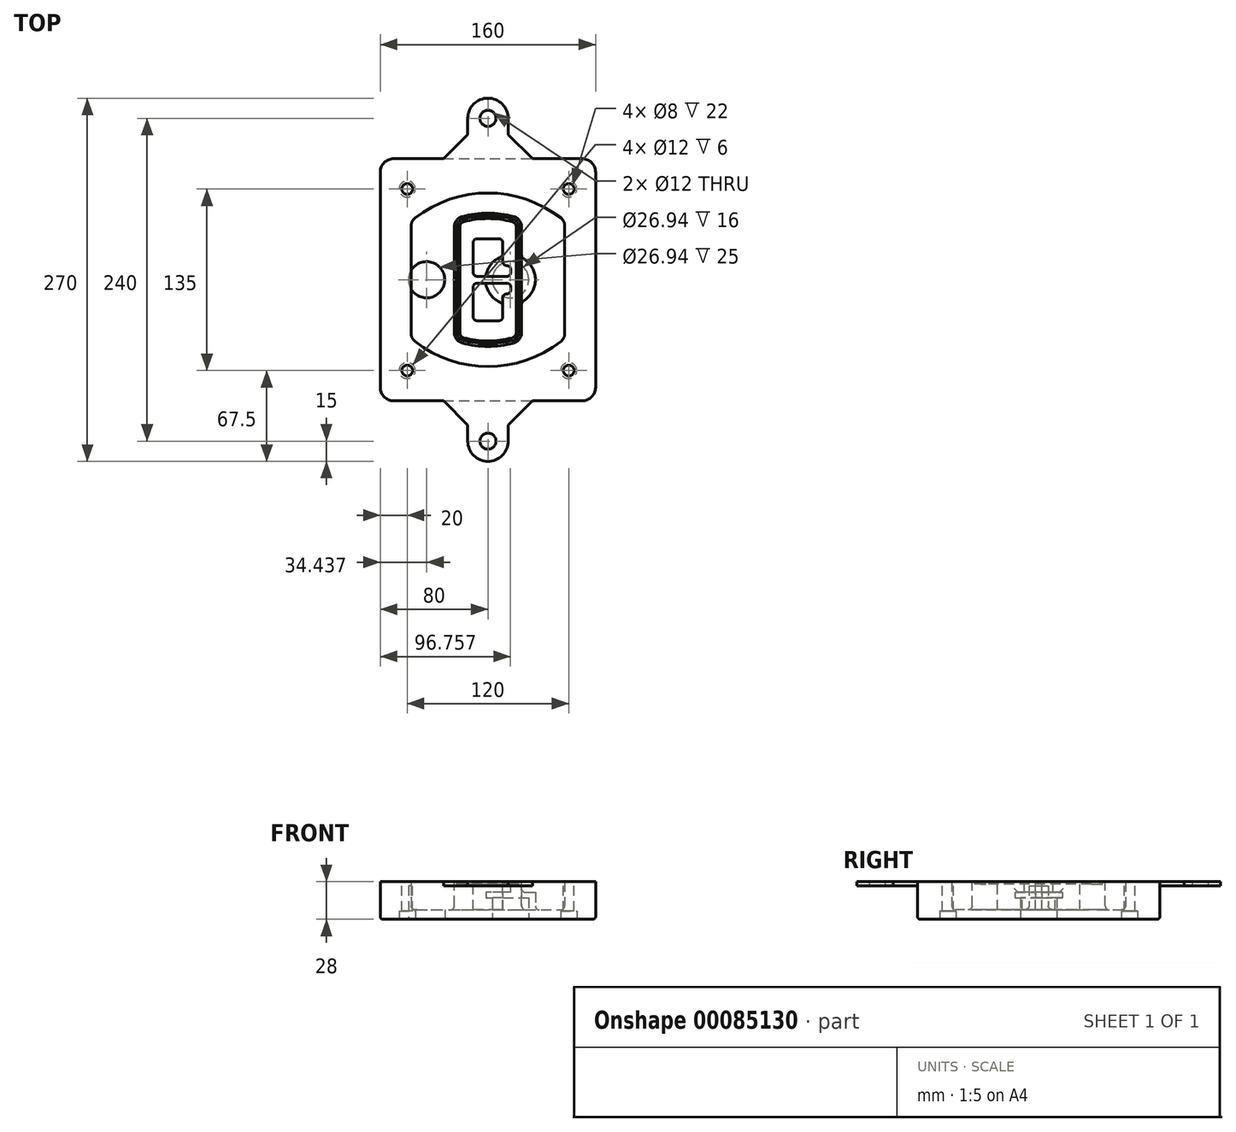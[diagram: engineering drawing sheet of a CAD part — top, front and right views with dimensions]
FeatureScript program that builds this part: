
annotation { "Feature Type Name" : "Feature", "Feature Type Description" : "" }
export const myFeature = defineFeature(function(context is Context, id is Id, definition is map)
    precondition{}
    {
        {
            var Q0;
            Q0=qCreatedBy(makeId("Top.planeOp"),FACE);
            var sketch = newSketch(context, id + "F0", { "sketchPlane" : qUnion([Q0])});
            skPoint(sketch, "E0.rect.middle", {"position": v(0, 0) * mm});
            skLineSegment(sketch, "E1.bottom", {"start": v(-70, -90) * mm, "end": v(70, -90) * mm});
            skLineSegment(sketch, "E1.top", {"start": v(-70, 90) * mm, "end": v(70, 90) * mm});
            skLineSegment(sketch, "E1.left", {"start": v(-80, -80) * mm, "end": v(-80, 80) * mm});
            skLineSegment(sketch, "E1.right", {"start": v(80, -80) * mm, "end": v(80, 80) * mm});
            skLineSegment(sketch, "E2", {"start": v(-80, 90) * mm, "end": v(80, -90) * mm, "construction": true});
            skLineSegment(sketch, "E3", {"start": v(80, 90) * mm, "end": v(-80, -90) * mm, "construction": true});
            skCircle(sketch, "E4", {"center": v(-60, 67.5) * mm, "radius": 4 * mm});
            skCircle(sketch, "E5", {"center": v(60, 67.5) * mm, "radius": 4 * mm});
            skCircle(sketch, "E6", {"center": v(60, -67.5) * mm, "radius": 4 * mm});
            skCircle(sketch, "E7", {"center": v(-60, -67.5) * mm, "radius": 4 * mm});
            skLineSegment(sketch, "E8", {"start": v(-60, 67.5) * mm, "end": v(60, 67.5) * mm, "construction": true});
            skLineSegment(sketch, "E9", {"start": v(60, 67.5) * mm, "end": v(60, -67.5) * mm, "construction": true});
            skLineSegment(sketch, "E10", {"start": v(60, -67.5) * mm, "end": v(-60, -67.5) * mm, "construction": true});
            skLineSegment(sketch, "E11", {"start": v(-60, -67.5) * mm, "end": v(-60, 67.5) * mm, "construction": true});
            skLineSegment(sketch, "E12", {"start": v(-60, 40.3) * mm, "end": v(-60, -40.3) * mm});
            skLineSegment(sketch, "E13", {"start": v(60, 40.3) * mm, "end": v(60, -40.3) * mm});
            skArc(sketch, "E14", {"start": v(56.15, 48.18) * mm, "mid": v(0, 67.5) * mm, "end": v(-56.15, 48.18) * mm});
            skArc(sketch, "E15", {"start": v(-56.15, -48.18) * mm, "mid": v(0, -67.5) * mm, "end": v(56.15, -48.18) * mm});
            skLineSegment(sketch, "E16", {"start": v(-60, 0) * mm, "end": v(60, 0) * mm, "construction": true});
            skPoint(sketch, "E17.visualSharp", {"position": v(-60, -45) * mm});
            skArc(sketch, "E17.filletArc", {"start": v(-60, -40.3) * mm, "mid": v(-58.99, -44.68) * mm, "end": v(-56.15, -48.18) * mm});
            skPoint(sketch, "E18.visualSharp", {"position": v(-60, 45) * mm});
            skArc(sketch, "E18.filletArc", {"start": v(-56.15, 48.18) * mm, "mid": v(-58.99, 44.68) * mm, "end": v(-60, 40.3) * mm});
            skPoint(sketch, "E19.visualSharp", {"position": v(60, 45) * mm});
            skArc(sketch, "E19.filletArc", {"start": v(60, 40.3) * mm, "mid": v(58.99, 44.68) * mm, "end": v(56.15, 48.18) * mm});
            skPoint(sketch, "E20.visualSharp", {"position": v(60, -45) * mm});
            skArc(sketch, "E20.filletArc", {"start": v(56.15, -48.18) * mm, "mid": v(58.99, -44.68) * mm, "end": v(60, -40.3) * mm});
            skPoint(sketch, "E21.visualSharp", {"position": v(-80, 90) * mm});
            skArc(sketch, "E21.filletArc", {"start": v(-70, 90) * mm, "mid": v(-77.07, 87.07) * mm, "end": v(-80, 80) * mm});
            skPoint(sketch, "E22.visualSharp", {"position": v(80, 90) * mm});
            skArc(sketch, "E22.filletArc", {"start": v(80, 80) * mm, "mid": v(77.07, 87.07) * mm, "end": v(70, 90) * mm});
            skPoint(sketch, "E23.visualSharp", {"position": v(80, -90) * mm});
            skArc(sketch, "E23.filletArc", {"start": v(70, -90) * mm, "mid": v(77.07, -87.07) * mm, "end": v(80, -80) * mm});
            skPoint(sketch, "E24.visualSharp", {"position": v(-80, -90) * mm});
            skArc(sketch, "E24.filletArc", {"start": v(-80, -80) * mm, "mid": v(-77.07, -87.07) * mm, "end": v(-70, -90) * mm});
            skArc(sketch, "E25.0", {"start": v(57, 40.3) * mm, "mid": v(56.3, 43.36) * mm, "end": v(54.3, 45.81) * mm});
            skLineSegment(sketch, "E25.1", {"start": v(57, 40.3) * mm, "end": v(57, -40.3) * mm});
            skArc(sketch, "E25.2", {"start": v(54.3, -45.81) * mm, "mid": v(56.3, -43.36) * mm, "end": v(57, -40.3) * mm});
            skArc(sketch, "E25.3", {"start": v(-54.3, -45.81) * mm, "mid": v(0, -64.5) * mm, "end": v(54.3, -45.81) * mm});
            skArc(sketch, "E25.4", {"start": v(-57, -40.3) * mm, "mid": v(-56.3, -43.36) * mm, "end": v(-54.3, -45.81) * mm});
            skArc(sketch, "E25.5", {"start": v(54.3, 45.81) * mm, "mid": v(0, 64.5) * mm, "end": v(-54.3, 45.81) * mm});
            skLineSegment(sketch, "E25.6", {"start": v(-57, 40.3) * mm, "end": v(-57, -40.3) * mm});
            skArc(sketch, "E25.7", {"start": v(-54.3, 45.81) * mm, "mid": v(-56.3, 43.36) * mm, "end": v(-57, 40.3) * mm});
            skArc(sketch, "E26.0", {"start": v(-58.62, 51.33) * mm, "mid": v(-62.58, 46.43) * mm, "end": v(-64, 40.3) * mm});
            skArc(sketch, "E26.1", {"start": v(58.62, 51.33) * mm, "mid": v(0, 71.5) * mm, "end": v(-58.62, 51.33) * mm});
            skArc(sketch, "E26.2", {"start": v(64, 40.3) * mm, "mid": v(62.58, 46.43) * mm, "end": v(58.62, 51.33) * mm});
            skLineSegment(sketch, "E26.3", {"start": v(64, 40.3) * mm, "end": v(64, -40.3) * mm});
            skArc(sketch, "E26.4", {"start": v(58.62, -51.33) * mm, "mid": v(62.58, -46.43) * mm, "end": v(64, -40.3) * mm});
            skLineSegment(sketch, "E26.5", {"start": v(-64, 40.3) * mm, "end": v(-64, -40.3) * mm});
            skArc(sketch, "E26.6", {"start": v(-58.62, -51.33) * mm, "mid": v(0, -71.5) * mm, "end": v(58.62, -51.33) * mm});
            skArc(sketch, "E26.7", {"start": v(-64, -40.3) * mm, "mid": v(-62.58, -46.43) * mm, "end": v(-58.62, -51.33) * mm});
            skSolve(sketch);
        }
        {
            var Q0;
            Q0=makeQuery(id+"F0.imprint","IMPRINT",FACE,{"disambiguationData":[TD([[makeQuery(id+"F0.imprint","IMPRINT",EDGE,{"derivedFrom":sQuery(id+"F0.wireOp",EDGE,"E1.bottom")}),1.0]])]});
            var Q1;
            Q1=makeQuery(id+"F0.imprint","IMPRINT",FACE,{"disambiguationData":[TD([[makeQuery(id+"F0.imprint","IMPRINT",EDGE,{"derivedFrom":sQuery(id+"F0.wireOp",EDGE,"E12")}),1.0]])]});
            var Q2;
            Q2=makeQuery(id+"F0.imprint","IMPRINT",FACE,{"disambiguationData":[TD([[makeQuery(id+"F0.imprint","IMPRINT",EDGE,{"derivedFrom":sQuery(id+"F0.wireOp",EDGE,"E25.0")}),1.0]])]});
            var Q3;
            Q3=makeQuery(id+"F0.imprint","IMPRINT",FACE,{"disambiguationData":[TD([[makeQuery(id+"F0.imprint","IMPRINT",EDGE,{"derivedFrom":sQuery(id+"F0.wireOp",EDGE,"E12")}),-1.0]])]});
            extrude(context, id + "F1", {"entities" : qUnion([Q0, Q1, Q2, Q3]), "oppositeDirection" : true, "depth" : 25 * mm});
        }
        {
            var Q0;
            Q0=makeQuery(id+"F0.imprint","IMPRINT",FACE,{"disambiguationData":[TD([[makeQuery(id+"F0.imprint","IMPRINT",EDGE,{"derivedFrom":sQuery(id+"F0.wireOp",EDGE,"E12")}),1.0]])]});
            extrude(context, id + "F2", {"entities" : qUnion([Q0]), "operationType" : NewBodyOperationType.ADD, "depth" : 3 * mm});
        }
        {
            var Q0;
            Q0=makeQuery(id+"F0.imprint","IMPRINT",FACE,{"disambiguationData":[TD([[makeQuery(id+"F0.imprint","IMPRINT",EDGE,{"derivedFrom":sQuery(id+"F0.wireOp",EDGE,"E25.0")}),1.0]])]});
            extrude(context, id + "F3", {"entities" : qUnion([Q0]), "operationType" : NewBodyOperationType.REMOVE, "oppositeDirection" : true, "depth" : 18 * mm});
        }
        {
            var Q0;
            Q0=makeQuery(id+"F2.opExtrude","CAP_FACE",FACE,{"disambiguationData":[OSD([sQuery(id+"F0.wireOp",EDGE,"E12"),sQuery(id+"F0.wireOp",EDGE,"E13"),sQuery(id+"F0.wireOp",EDGE,"E14"),sQuery(id+"F0.wireOp",EDGE,"E15"),sQuery(id+"F0.wireOp",EDGE,"E17.filletArc"),sQuery(id+"F0.wireOp",EDGE,"E18.filletArc"),sQuery(id+"F0.wireOp",EDGE,"E19.filletArc"),sQuery(id+"F0.wireOp",EDGE,"E20.filletArc"),sQuery(id+"F0.wireOp",EDGE,"E25.0"),sQuery(id+"F0.wireOp",EDGE,"E25.1"),sQuery(id+"F0.wireOp",EDGE,"E25.2"),sQuery(id+"F0.wireOp",EDGE,"E25.3"),sQuery(id+"F0.wireOp",EDGE,"E25.4"),sQuery(id+"F0.wireOp",EDGE,"E25.5"),sQuery(id+"F0.wireOp",EDGE,"E25.6"),sQuery(id+"F0.wireOp",EDGE,"E25.7")])],"isStart":false});
            var sketch = newSketch(context, id + "F4", { "sketchPlane" : qUnion([Q0])});
            skArc(sketch, "E27.0", {"start": v(-19.08, -46.97) * mm, "mid": v(0, -49.5) * mm, "end": v(19.08, -46.97) * mm});
            skArc(sketch, "E28.0", {"start": v(19.08, 46.97) * mm, "mid": v(0, 49.5) * mm, "end": v(-19.08, 46.97) * mm});
            skLineSegment(sketch, "E29", {"start": v(-25, 39.25) * mm, "end": v(-25, -39.25) * mm});
            skLineSegment(sketch, "E30", {"start": v(25, 39.25) * mm, "end": v(25, -39.25) * mm});
            skLineSegment(sketch, "E31", {"start": v(-25, 45.1) * mm, "end": v(25, 45.1) * mm, "construction": true});
            skLineSegment(sketch, "E32", {"start": v(-25, -45.1) * mm, "end": v(25, -45.1) * mm, "construction": true});
            skPoint(sketch, "E33.visualSharp", {"position": v(-25, 45.1) * mm});
            skArc(sketch, "E33.filletArc", {"start": v(-19.08, 46.97) * mm, "mid": v(-23.35, 44.11) * mm, "end": v(-25, 39.25) * mm});
            skPoint(sketch, "E34.visualSharp", {"position": v(25, 45.1) * mm});
            skArc(sketch, "E34.filletArc", {"start": v(25, 39.25) * mm, "mid": v(23.35, 44.11) * mm, "end": v(19.08, 46.97) * mm});
            skPoint(sketch, "E35.visualSharp", {"position": v(25, -45.1) * mm});
            skArc(sketch, "E35.filletArc", {"start": v(19.08, -46.97) * mm, "mid": v(23.35, -44.11) * mm, "end": v(25, -39.25) * mm});
            skPoint(sketch, "E36.visualSharp", {"position": v(-25, -45.1) * mm});
            skArc(sketch, "E36.filletArc", {"start": v(-25, -39.25) * mm, "mid": v(-23.35, -44.11) * mm, "end": v(-19.08, -46.97) * mm});
            skArc(sketch, "E37.0", {"start": v(54.3, 45.81) * mm, "mid": v(0, 64.5) * mm, "end": v(-54.3, 45.81) * mm});
            skArc(sketch, "E37.1", {"start": v(-54.3, 45.81) * mm, "mid": v(-56.3, 43.36) * mm, "end": v(-57, 40.3) * mm});
            skLineSegment(sketch, "E37.2", {"start": v(-57, 40.3) * mm, "end": v(-57, -40.3) * mm});
            skArc(sketch, "E37.3", {"start": v(-57, -40.3) * mm, "mid": v(-56.3, -43.36) * mm, "end": v(-54.3, -45.81) * mm});
            skArc(sketch, "E37.4", {"start": v(-54.3, -45.81) * mm, "mid": v(0, -64.5) * mm, "end": v(54.3, -45.81) * mm});
            skArc(sketch, "E37.5", {"start": v(54.3, -45.81) * mm, "mid": v(56.3, -43.36) * mm, "end": v(57, -40.3) * mm});
            skLineSegment(sketch, "E37.6", {"start": v(57, 40.3) * mm, "end": v(57, -40.3) * mm});
            skArc(sketch, "E37.7", {"start": v(57, 40.3) * mm, "mid": v(56.3, 43.36) * mm, "end": v(54.3, 45.81) * mm});
            skLineSegment(sketch, "E38.0", {"start": v(23, 39.25) * mm, "end": v(23, -39.25) * mm});
            skArc(sketch, "E38.1", {"start": v(18.56, -45.04) * mm, "mid": v(21.76, -42.9) * mm, "end": v(23, -39.25) * mm});
            skArc(sketch, "E38.2", {"start": v(-18.56, -45.04) * mm, "mid": v(0, -47.5) * mm, "end": v(18.56, -45.04) * mm});
            skArc(sketch, "E38.3", {"start": v(-23, -39.25) * mm, "mid": v(-21.76, -42.9) * mm, "end": v(-18.56, -45.04) * mm});
            skLineSegment(sketch, "E38.4", {"start": v(-23, 39.25) * mm, "end": v(-23, -39.25) * mm});
            skArc(sketch, "E38.5", {"start": v(23, 39.25) * mm, "mid": v(21.76, 42.9) * mm, "end": v(18.56, 45.04) * mm});
            skArc(sketch, "E38.6", {"start": v(-18.56, 45.04) * mm, "mid": v(-21.76, 42.9) * mm, "end": v(-23, 39.25) * mm});
            skArc(sketch, "E38.7", {"start": v(18.56, 45.04) * mm, "mid": v(0, 47.5) * mm, "end": v(-18.56, 45.04) * mm});
            skArc(sketch, "E39.0", {"start": v(21, 39.25) * mm, "mid": v(20.18, 41.68) * mm, "end": v(18.04, 43.1) * mm});
            skLineSegment(sketch, "E39.1", {"start": v(21, 39.25) * mm, "end": v(21, -39.25) * mm});
            skArc(sketch, "E39.2", {"start": v(18.04, -43.1) * mm, "mid": v(20.18, -41.68) * mm, "end": v(21, -39.25) * mm});
            skArc(sketch, "E39.3", {"start": v(-18.04, -43.1) * mm, "mid": v(0, -45.5) * mm, "end": v(18.04, -43.1) * mm});
            skArc(sketch, "E39.4", {"start": v(-21, -39.25) * mm, "mid": v(-20.18, -41.68) * mm, "end": v(-18.04, -43.1) * mm});
            skArc(sketch, "E39.5", {"start": v(18.04, 43.1) * mm, "mid": v(0, 45.5) * mm, "end": v(-18.04, 43.1) * mm});
            skLineSegment(sketch, "E39.6", {"start": v(-21, 39.25) * mm, "end": v(-21, -39.25) * mm});
            skArc(sketch, "E39.7", {"start": v(-18.04, 43.1) * mm, "mid": v(-20.18, 41.68) * mm, "end": v(-21, 39.25) * mm});
            skLineSegment(sketch, "E40", {"start": v(-25, 0) * mm, "end": v(25, 0) * mm, "construction": true});
            skLineSegment(sketch, "E41", {"start": v(-11, 5.5) * mm, "end": v(-11, 27.5) * mm});
            skLineSegment(sketch, "E42", {"start": v(-8, 30.5) * mm, "end": v(8, 30.5) * mm});
            skLineSegment(sketch, "E43", {"start": v(11, 27.5) * mm, "end": v(11, 13.5) * mm});
            skLineSegment(sketch, "E44", {"start": v(14, 10.5) * mm, "end": v(14, 10.5) * mm});
            skLineSegment(sketch, "E45", {"start": v(17, 7.5) * mm, "end": v(17, 5.5) * mm});
            skLineSegment(sketch, "E46", {"start": v(14, 2.5) * mm, "end": v(-8, 2.5) * mm});
            skPoint(sketch, "E47.visualSharp", {"position": v(-11, 30.5) * mm});
            skArc(sketch, "E47.filletArc", {"start": v(-8, 30.5) * mm, "mid": v(-10.12, 29.62) * mm, "end": v(-11, 27.5) * mm});
            skPoint(sketch, "E48.visualSharp", {"position": v(11, 30.5) * mm});
            skArc(sketch, "E48.filletArc", {"start": v(11, 27.5) * mm, "mid": v(10.12, 29.62) * mm, "end": v(8, 30.5) * mm});
            skPoint(sketch, "E49.visualSharp", {"position": v(11, 10.5) * mm});
            skArc(sketch, "E49.filletArc", {"start": v(11, 13.5) * mm, "mid": v(11.88, 11.38) * mm, "end": v(14, 10.5) * mm});
            skPoint(sketch, "E50.visualSharp", {"position": v(17, 10.5) * mm});
            skArc(sketch, "E50.filletArc", {"start": v(17, 7.5) * mm, "mid": v(16.12, 9.62) * mm, "end": v(14, 10.5) * mm});
            skPoint(sketch, "E51.visualSharp", {"position": v(17, 2.5) * mm});
            skArc(sketch, "E51.filletArc", {"start": v(14, 2.5) * mm, "mid": v(16.12, 3.38) * mm, "end": v(17, 5.5) * mm});
            skPoint(sketch, "E52.visualSharp", {"position": v(-11, 2.5) * mm});
            skArc(sketch, "E52.filletArc", {"start": v(-11, 5.5) * mm, "mid": v(-10.12, 3.38) * mm, "end": v(-8, 2.5) * mm});
            skLineSegment(sketch, "E53.0.MirrorCS", {"start": v(14, -2.5) * mm, "end": v(-8, -2.5) * mm});
            skArc(sketch, "E54.0.MirrorCS", {"start": v(-11, -5.5) * mm, "mid": v(-10.12, -3.38) * mm, "end": v(-8, -2.5) * mm});
            skLineSegment(sketch, "E55.0.MirrorCS", {"start": v(-11, -5.5) * mm, "end": v(-11, -27.5) * mm});
            skArc(sketch, "E56.0.MirrorCS", {"start": v(-8, -30.5) * mm, "mid": v(-10.12, -29.62) * mm, "end": v(-11, -27.5) * mm});
            skLineSegment(sketch, "E57.0.MirrorCS", {"start": v(-8, -30.5) * mm, "end": v(8, -30.5) * mm});
            skArc(sketch, "E58.0.MirrorCS", {"start": v(11, -27.5) * mm, "mid": v(10.12, -29.62) * mm, "end": v(8, -30.5) * mm});
            skLineSegment(sketch, "E59.0.MirrorCS", {"start": v(11, -27.5) * mm, "end": v(11, -13.5) * mm});
            skArc(sketch, "E60.0.MirrorCS", {"start": v(11, -13.5) * mm, "mid": v(11.88, -11.38) * mm, "end": v(14, -10.5) * mm});
            skArc(sketch, "E61.0.MirrorCS", {"start": v(17, -7.5) * mm, "mid": v(16.12, -9.62) * mm, "end": v(14, -10.5) * mm});
            skLineSegment(sketch, "E62.0.MirrorCS", {"start": v(17, -7.5) * mm, "end": v(17, -5.5) * mm});
            skArc(sketch, "E63.0.MirrorCS", {"start": v(14, -2.5) * mm, "mid": v(16.12, -3.38) * mm, "end": v(17, -5.5) * mm});
            skSolve(sketch);
        }
        {
            var Q0;
            Q0=makeQuery(id+"F4.imprint","IMPRINT",FACE,{"disambiguationData":[TD([[makeQuery(id+"F4.imprint","IMPRINT",EDGE,{"derivedFrom":sQuery(id+"F4.wireOp",EDGE,"E27.0")}),1.0]])]});
            var Q1;
            Q1=makeQuery(id+"F4.imprint","IMPRINT",FACE,{"disambiguationData":[TD([[makeQuery(id+"F4.imprint","IMPRINT",EDGE,{"derivedFrom":sQuery(id+"F4.wireOp",EDGE,"E38.0")}),-1.0]])]});
            var Q2;
            Q2=makeQuery(id+"F4.imprint","IMPRINT",FACE,{"disambiguationData":[TD([[makeQuery(id+"F4.imprint","IMPRINT",EDGE,{"derivedFrom":sQuery(id+"F4.wireOp",EDGE,"E39.0")}),1.0]])]});
            extrude(context, id + "F5", {"entities" : qUnion([Q0, Q1, Q2]), "operationType" : NewBodyOperationType.ADD, "endBound" : BoundingType.UP_TO_NEXT, "oppositeDirection" : true, "depth" : 25 * mm});
        }
        {
            var Q0;
            Q0=makeQuery(id+"F4.imprint","IMPRINT",FACE,{"disambiguationData":[TD([[makeQuery(id+"F4.imprint","IMPRINT",EDGE,{"derivedFrom":sQuery(id+"F4.wireOp",EDGE,"E38.0")}),-1.0]])]});
            extrude(context, id + "F6", {"entities" : qUnion([Q0]), "operationType" : NewBodyOperationType.REMOVE, "oppositeDirection" : true, "depth" : 2 * mm});
        }
        {
            var Q0;
            Q0=makeQuery(id+"F1.opExtrude","CAP_FACE",FACE,{"disambiguationData":[OSD([sQuery(id+"F0.wireOp",EDGE,"E1.bottom"),sQuery(id+"F0.wireOp",EDGE,"E1.top"),sQuery(id+"F0.wireOp",EDGE,"E1.left"),sQuery(id+"F0.wireOp",EDGE,"E1.right"),sQuery(id+"F0.wireOp",EDGE,"E4"),sQuery(id+"F0.wireOp",EDGE,"E5"),sQuery(id+"F0.wireOp",EDGE,"E6"),sQuery(id+"F0.wireOp",EDGE,"E7"),sQuery(id+"F0.wireOp",EDGE,"E21.filletArc"),sQuery(id+"F0.wireOp",EDGE,"E22.filletArc"),sQuery(id+"F0.wireOp",EDGE,"E23.filletArc"),sQuery(id+"F0.wireOp",EDGE,"E24.filletArc")])],"isStart":false});
            var sketch = newSketch(context, id + "F7", { "sketchPlane" : qUnion([Q0])});
            skCircle(sketch, "E64", {"center": v(16.76, 0) * mm, "radius": 13.47 * mm});
            skCircle(sketch, "E65", {"center": v(-45.56, 0) * mm, "radius": 13.47 * mm});
            skLineSegment(sketch, "E66", {"start": v(80, 0) * mm, "end": v(-80, 0) * mm});
            skCircle(sketch, "E67", {"center": v(16.76, 0) * mm, "radius": 18.47 * mm});
            skCircle(sketch, "E68", {"center": v(60, -67.5) * mm, "radius": 6 * mm});
            skCircle(sketch, "E69", {"center": v(-60, -67.5) * mm, "radius": 6 * mm});
            skCircle(sketch, "E70", {"center": v(-60, 67.5) * mm, "radius": 6 * mm});
            skCircle(sketch, "E71", {"center": v(60, 67.5) * mm, "radius": 6 * mm});
            skSolve(sketch);
        }
        {
            var Q0;
            {var subQ1=sQuery(id+"F7.wireOp",EDGE,"E66");var subQ4=sQuery(id+"F7.wireOp",EDGE,"E64");var subQ6=makeQuery(id+"F7.imprint","INTERSECT",VERTEX,{"disambiguationData":[OD(0.0)],"derivedFrom":[subQ4,subQ1]});Q0=makeQuery(id+"F7.imprint","IMPRINT",FACE,{"disambiguationData":[TD([[makeQuery(id+"F7.imprint","IMPRINT",EDGE,{"disambiguationData":[TD([[subQ6,-1.0]])],"derivedFrom":subQ4}),-1.0]])]});}
            var Q1;
            {var subQ0=sQuery(id+"F7.wireOp",EDGE,"E66");var subQ1=sQuery(id+"F7.wireOp",EDGE,"E64");var subQ3=makeQuery(id+"F7.imprint","INTERSECT",VERTEX,{"disambiguationData":[OD(0.0)],"derivedFrom":[subQ1,subQ0]});Q1=makeQuery(id+"F7.imprint","IMPRINT",FACE,{"disambiguationData":[TD([[makeQuery(id+"F7.imprint","IMPRINT",EDGE,{"disambiguationData":[TD([[subQ3,-1.0]])],"derivedFrom":subQ1}),1.0]])]});}
            var Q2;
            {var subQ0=sQuery(id+"F7.wireOp",EDGE,"E66");var subQ1=sQuery(id+"F7.wireOp",EDGE,"E64");var subQ3=makeQuery(id+"F7.imprint","INTERSECT",VERTEX,{"disambiguationData":[OD(0.0)],"derivedFrom":[subQ1,subQ0]});Q2=makeQuery(id+"F7.imprint","IMPRINT",FACE,{"disambiguationData":[TD([[makeQuery(id+"F7.imprint","IMPRINT",EDGE,{"disambiguationData":[TD([[subQ3,1.0]])],"derivedFrom":subQ1}),1.0]])]});}
            var Q3;
            {var subQ1=sQuery(id+"F7.wireOp",EDGE,"E66");var subQ4=sQuery(id+"F7.wireOp",EDGE,"E64");var subQ6=makeQuery(id+"F7.imprint","INTERSECT",VERTEX,{"disambiguationData":[OD(0.0)],"derivedFrom":[subQ4,subQ1]});Q3=makeQuery(id+"F7.imprint","IMPRINT",FACE,{"disambiguationData":[TD([[makeQuery(id+"F7.imprint","IMPRINT",EDGE,{"disambiguationData":[TD([[subQ6,1.0]])],"derivedFrom":subQ4}),-1.0]])]});}
            extrude(context, id + "F8", {"entities" : qUnion([Q0, Q1, Q2, Q3]), "operationType" : NewBodyOperationType.ADD, "oppositeDirection" : true, "depth" : 20 * mm});
        }
        {
            var Q0;
            {var subQ0=sQuery(id+"F7.wireOp",EDGE,"E66");var subQ1=sQuery(id+"F7.wireOp",EDGE,"E64");var subQ3=makeQuery(id+"F7.imprint","INTERSECT",VERTEX,{"disambiguationData":[OD(0.0)],"derivedFrom":[subQ1,subQ0]});Q0=makeQuery(id+"F7.imprint","IMPRINT",FACE,{"disambiguationData":[TD([[makeQuery(id+"F7.imprint","IMPRINT",EDGE,{"disambiguationData":[TD([[subQ3,-1.0]])],"derivedFrom":subQ1}),1.0]])]});}
            var Q1;
            {var subQ0=sQuery(id+"F7.wireOp",EDGE,"E66");var subQ1=sQuery(id+"F7.wireOp",EDGE,"E64");var subQ3=makeQuery(id+"F7.imprint","INTERSECT",VERTEX,{"disambiguationData":[OD(0.0)],"derivedFrom":[subQ1,subQ0]});Q1=makeQuery(id+"F7.imprint","IMPRINT",FACE,{"disambiguationData":[TD([[makeQuery(id+"F7.imprint","IMPRINT",EDGE,{"disambiguationData":[TD([[subQ3,1.0]])],"derivedFrom":subQ1}),1.0]])]});}
            extrude(context, id + "F9", {"entities" : qUnion([Q0, Q1]), "operationType" : NewBodyOperationType.REMOVE, "oppositeDirection" : true, "depth" : 16 * mm});
        }
        {
            var Q0;
            {var subQ0=sQuery(id+"F7.wireOp",EDGE,"E66");var subQ1=sQuery(id+"F7.wireOp",EDGE,"E65");var subQ3=makeQuery(id+"F7.imprint","INTERSECT",VERTEX,{"disambiguationData":[OD(0.0)],"derivedFrom":[subQ1,subQ0]});Q0=makeQuery(id+"F7.imprint","IMPRINT",FACE,{"disambiguationData":[TD([[makeQuery(id+"F7.imprint","IMPRINT",EDGE,{"disambiguationData":[TD([[subQ3,-1.0]])],"derivedFrom":subQ1}),1.0]])]});}
            var Q1;
            {var subQ0=sQuery(id+"F7.wireOp",EDGE,"E66");var subQ1=sQuery(id+"F7.wireOp",EDGE,"E65");var subQ3=makeQuery(id+"F7.imprint","INTERSECT",VERTEX,{"disambiguationData":[OD(0.0)],"derivedFrom":[subQ1,subQ0]});Q1=makeQuery(id+"F7.imprint","IMPRINT",FACE,{"disambiguationData":[TD([[makeQuery(id+"F7.imprint","IMPRINT",EDGE,{"disambiguationData":[TD([[subQ3,1.0]])],"derivedFrom":subQ1}),1.0]])]});}
            extrude(context, id + "F10", {"entities" : qUnion([Q0, Q1]), "operationType" : NewBodyOperationType.REMOVE, "oppositeDirection" : true, "depth" : 25 * mm});
        }
        {
            var Q0;
            Q0=makeQuery(id+"F7.imprint","IMPRINT",FACE,{"disambiguationData":[TD([[makeQuery(id+"F7.imprint","IMPRINT",EDGE,{"derivedFrom":sQuery(id+"F7.wireOp",EDGE,"E68")}),1.0]])]});
            var Q1;
            Q1=makeQuery(id+"F7.imprint","IMPRINT",FACE,{"disambiguationData":[TD([[makeQuery(id+"F7.imprint","IMPRINT",EDGE,{"derivedFrom":makeQuery(id+"F1.opExtrude","CAP_EDGE",EDGE,{"disambiguationData":[OSD([sQuery(id+"F0.wireOp",EDGE,"E5")])],"isStart":false})}),-1.0]])]});
            var Q2;
            Q2=makeQuery(id+"F7.imprint","IMPRINT",FACE,{"disambiguationData":[TD([[makeQuery(id+"F7.imprint","IMPRINT",EDGE,{"derivedFrom":sQuery(id+"F7.wireOp",EDGE,"E69")}),1.0]])]});
            var Q3;
            Q3=makeQuery(id+"F7.imprint","IMPRINT",FACE,{"disambiguationData":[TD([[makeQuery(id+"F7.imprint","IMPRINT",EDGE,{"derivedFrom":makeQuery(id+"F1.opExtrude","CAP_EDGE",EDGE,{"disambiguationData":[OSD([sQuery(id+"F0.wireOp",EDGE,"E4")])],"isStart":false})}),-1.0]])]});
            var Q4;
            Q4=makeQuery(id+"F7.imprint","IMPRINT",FACE,{"disambiguationData":[TD([[makeQuery(id+"F7.imprint","IMPRINT",EDGE,{"derivedFrom":sQuery(id+"F7.wireOp",EDGE,"E70")}),1.0]])]});
            var Q5;
            Q5=makeQuery(id+"F7.imprint","IMPRINT",FACE,{"disambiguationData":[TD([[makeQuery(id+"F7.imprint","IMPRINT",EDGE,{"derivedFrom":makeQuery(id+"F1.opExtrude","CAP_EDGE",EDGE,{"disambiguationData":[OSD([sQuery(id+"F0.wireOp",EDGE,"E7")])],"isStart":false})}),-1.0]])]});
            var Q6;
            Q6=makeQuery(id+"F7.imprint","IMPRINT",FACE,{"disambiguationData":[TD([[makeQuery(id+"F7.imprint","IMPRINT",EDGE,{"derivedFrom":sQuery(id+"F7.wireOp",EDGE,"E71")}),1.0]])]});
            var Q7;
            Q7=makeQuery(id+"F7.imprint","IMPRINT",FACE,{"disambiguationData":[TD([[makeQuery(id+"F7.imprint","IMPRINT",EDGE,{"derivedFrom":makeQuery(id+"F1.opExtrude","CAP_EDGE",EDGE,{"disambiguationData":[OSD([sQuery(id+"F0.wireOp",EDGE,"E6")])],"isStart":false})}),-1.0]])]});
            extrude(context, id + "F11", {"entities" : qUnion([Q0, Q1, Q2, Q3, Q4, Q5, Q6, Q7]), "operationType" : NewBodyOperationType.REMOVE, "oppositeDirection" : true, "depth" : 6 * mm});
        }
        {
            var Q0;
            Q0=makeQuery(id+"F9.boolean.opBoolean","COPY",FACE,{"derivedFrom":makeQuery(id+"F9.opExtrude","CAP_FACE",FACE,{"disambiguationData":[OSD([sQuery(id+"F7.wireOp",EDGE,"E64")])],"isStart":false})});
            var sketch = newSketch(context, id + "F12", { "sketchPlane" : qUnion([Q0])});
            skArc(sketch, "E72.0", {"start": v(11, 17.55) * mm, "mid": v(2.57, 11.82) * mm, "end": v(-1.54, 2.5) * mm});
            skArc(sketch, "E72.1", {"start": v(-1.54, -2.5) * mm, "mid": v(2.57, -11.82) * mm, "end": v(11, -17.55) * mm});
            skLineSegment(sketch, "E73", {"start": v(-1.54, -2.5) * mm, "end": v(14, -2.5) * mm});
            skLineSegment(sketch, "E74.0", {"start": v(14, 2.5) * mm, "end": v(-1.54, 2.5) * mm});
            skArc(sketch, "E74.1", {"start": v(14, 2.5) * mm, "mid": v(16.12, 3.38) * mm, "end": v(17, 5.5) * mm});
            skLineSegment(sketch, "E74.2", {"start": v(17, 7.5) * mm, "end": v(17, 5.5) * mm});
            skArc(sketch, "E74.3", {"start": v(17, 7.5) * mm, "mid": v(16.12, 9.62) * mm, "end": v(14, 10.5) * mm});
            skArc(sketch, "E74.4", {"start": v(11, 13.5) * mm, "mid": v(11.88, 11.38) * mm, "end": v(14, 10.5) * mm});
            skLineSegment(sketch, "E74.5", {"start": v(11, 17.55) * mm, "end": v(11, 13.5) * mm});
            skLineSegment(sketch, "E74.7", {"start": v(14, -2.5) * mm, "end": v(-1.54, -2.5) * mm});
            skArc(sketch, "E74.8", {"start": v(14, -2.5) * mm, "mid": v(16.12, -3.38) * mm, "end": v(17, -5.5) * mm});
            skLineSegment(sketch, "E74.9", {"start": v(17, -7.5) * mm, "end": v(17, -5.5) * mm});
            skArc(sketch, "E74.10", {"start": v(17, -7.5) * mm, "mid": v(16.12, -9.62) * mm, "end": v(14, -10.5) * mm});
            skArc(sketch, "E74.11", {"start": v(11, -13.5) * mm, "mid": v(11.88, -11.38) * mm, "end": v(14, -10.5) * mm});
            skLineSegment(sketch, "E74.12", {"start": v(11, -17.55) * mm, "end": v(11, -13.5) * mm});
            skPoint(sketch, "E75.orphan", {"position": v(11, -27.5) * mm});
            skPoint(sketch, "E76.orphan", {"position": v(-8, -2.5) * mm});
            skPoint(sketch, "E77.orphan", {"position": v(-8, 2.5) * mm});
            skPoint(sketch, "E78.orphan", {"position": v(11, 27.5) * mm});
            skSolve(sketch);
        }
        {
            var Q0;
            {var subQ7=sQuery(id+"F12.wireOp",EDGE,"E72.0");var subQ14=sQuery(id+"F12.wireOp",EDGE,"E72.1");var subQ16=sQuery(id+"F12.wireOp",EDGE,"E74.1");var subQ18=sQuery(id+"F12.wireOp",EDGE,"E74.8");Q0=qUnion([makeQuery(id+"F12.imprint","IMPRINT",FACE,{"disambiguationData":[TD([[makeQuery(id+"F12.imprint","IMPRINT",EDGE,{"derivedFrom":subQ7}),1.0]])]}),makeQuery(id+"F12.imprint","IMPRINT",FACE,{"disambiguationData":[TD([[makeQuery(id+"F12.imprint","IMPRINT",EDGE,{"derivedFrom":subQ14}),1.0]])]}),makeQuery(id+"F12.imprint","IMPRINT",FACE,{"disambiguationData":[TD([[makeQuery(id+"F12.imprint","IMPRINT",EDGE,{"derivedFrom":subQ16}),1.0]])]}),makeQuery(id+"F12.imprint","IMPRINT",FACE,{"disambiguationData":[TD([[makeQuery(id+"F12.imprint","IMPRINT",EDGE,{"derivedFrom":subQ18}),-1.0]])]})]);}
            var Q1;
            Q1=makeQuery(id+"F5.boolean.opBoolean","SPLIT",FACE,{"disambiguationData":[TD([makeQuery(id+"F5.opExtrude","SWEPT_FACE",FACE,{"disambiguationData":[OSD([sQuery(id+"F4.wireOp",EDGE,"E41")])]})])],"derivedFrom":makeQuery(id+"F3.boolean.opBoolean","COPY",FACE,{"derivedFrom":makeQuery(id+"F3.opExtrude","CAP_FACE",FACE,{"disambiguationData":[OSD([sQuery(id+"F0.wireOp",EDGE,"E25.0"),sQuery(id+"F0.wireOp",EDGE,"E25.1"),sQuery(id+"F0.wireOp",EDGE,"E25.2"),sQuery(id+"F0.wireOp",EDGE,"E25.3"),sQuery(id+"F0.wireOp",EDGE,"E25.4"),sQuery(id+"F0.wireOp",EDGE,"E25.5"),sQuery(id+"F0.wireOp",EDGE,"E25.6"),sQuery(id+"F0.wireOp",EDGE,"E25.7")])],"isStart":false})})});
            extrude(context, id + "F13", {"entities" : qUnion([Q0]), "operationType" : NewBodyOperationType.REMOVE, "endBound" : BoundingType.UP_TO_SURFACE, "endBoundEntityFace" : qUnion([Q1]), "depth" : 25 * mm});
        }
        {
            var Q0;
            Q0=makeQuery(id+"F3.boolean.opBoolean","COPY",EDGE,{"derivedFrom":makeQuery(id+"F3.opExtrude","CAP_EDGE",EDGE,{"disambiguationData":[OSD([sQuery(id+"F0.wireOp",EDGE,"E25.6")])],"isStart":false})});
            var Q1;
            Q1=makeQuery(id+"F8.boolean.opBoolean","INTERSECT",EDGE,{"derivedFrom":[makeQuery(id+"F5.opExtrude","SWEPT_FACE",FACE,{"disambiguationData":[OSD([sQuery(id+"F4.wireOp",EDGE,"E30")])]}),makeQuery(id+"F8.opExtrude","CAP_FACE",FACE,{"disambiguationData":[OSD([sQuery(id+"F7.wireOp",EDGE,"E67")])],"isStart":false})]});
            var Q2;
            Q2=makeQuery(id+"F8.boolean.opBoolean","INTERSECT",EDGE,{"disambiguationData":[OD(1.0)],"derivedFrom":[makeQuery(id+"F5.opExtrude","SWEPT_FACE",FACE,{"disambiguationData":[OSD([sQuery(id+"F4.wireOp",EDGE,"E30")])]}),makeQuery(id+"F8.opExtrude","SWEPT_FACE",FACE,{"disambiguationData":[OSD([sQuery(id+"F7.wireOp",EDGE,"E67")])]})]});
            var Q3;
            {var subQ0=sQuery(id+"F4.wireOp",EDGE,"E30");Q3=makeQuery(id+"F8.boolean.opBoolean","SPLIT",EDGE,{"disambiguationData":[TD([makeQuery(id+"F5.opExtrude","SWEPT_FACE",FACE,{"disambiguationData":[OSD([sQuery(id+"F4.wireOp",EDGE,"E35.filletArc")])]})])],"derivedFrom":makeQuery(id+"F5.opExtrude","CAP_EDGE",EDGE,{"disambiguationData":[OSD([subQ0])],"isStart":false})});}
            var Q4;
            {var subQ0=sQuery(id+"F0.wireOp",EDGE,"E25.7");var subQ1=sQuery(id+"F0.wireOp",EDGE,"E25.1");var subQ2=sQuery(id+"F0.wireOp",EDGE,"E25.6");var subQ3=sQuery(id+"F0.wireOp",EDGE,"E25.5");var subQ4=sQuery(id+"F0.wireOp",EDGE,"E25.4");var subQ5=sQuery(id+"F0.wireOp",EDGE,"E25.0");var subQ6=sQuery(id+"F0.wireOp",EDGE,"E25.2");var subQ7=sQuery(id+"F0.wireOp",EDGE,"E25.3");Q4=makeQuery(id+"F8.boolean.opBoolean","INTERSECT",EDGE,{"derivedFrom":[makeQuery(id+"F5.boolean.opBoolean","SPLIT",FACE,{"disambiguationData":[TD([makeQuery(id+"F2.opExtrude","SWEPT_FACE",FACE,{"disambiguationData":[OSD([subQ5])]})])],"derivedFrom":makeQuery(id+"F3.boolean.opBoolean","COPY",FACE,{"derivedFrom":makeQuery(id+"F3.opExtrude","CAP_FACE",FACE,{"disambiguationData":[OSD([subQ5,subQ1,subQ6,subQ7,subQ4,subQ3,subQ2,subQ0])],"isStart":false})})}),makeQuery(id+"F8.opExtrude","SWEPT_FACE",FACE,{"disambiguationData":[OSD([sQuery(id+"F7.wireOp",EDGE,"E67")])]})]});}
            var Q5;
            Q5=makeQuery(id+"F8.boolean.opBoolean","INTERSECT",EDGE,{"disambiguationData":[OD(0.0)],"derivedFrom":[makeQuery(id+"F5.opExtrude","SWEPT_FACE",FACE,{"disambiguationData":[OSD([sQuery(id+"F4.wireOp",EDGE,"E30")])]}),makeQuery(id+"F8.opExtrude","SWEPT_FACE",FACE,{"disambiguationData":[OSD([sQuery(id+"F7.wireOp",EDGE,"E67")])]})]});
            fillet(context, id + "F14", {"entities" : qUnion([Q0, Q1, Q2, Q3, Q4, Q5]), "radius" : 3 * mm, "tangentPropagation" : true, "allowEdgeOverflow" : false});
        }
        {
            var Q0;
            Q0=makeQuery(id+"F1.opExtrude","CAP_EDGE",EDGE,{"disambiguationData":[OSD([sQuery(id+"F0.wireOp",EDGE,"E1.bottom")])],"isStart":false});
            fillet(context, id + "F15", {"entities" : qUnion([Q0]), "radius" : 2 * mm, "tangentPropagation" : true, "allowEdgeOverflow" : false});
        }
        {
            var Q0;
            {var subQ0=sQuery(id+"F0.wireOp",EDGE,"E22.filletArc");var subQ1=sQuery(id+"F0.wireOp",EDGE,"E7");var subQ2=sQuery(id+"F0.wireOp",EDGE,"E6");var subQ3=sQuery(id+"F0.wireOp",EDGE,"E5");var subQ4=sQuery(id+"F0.wireOp",EDGE,"E4");var subQ5=sQuery(id+"F0.wireOp",EDGE,"E1.bottom");var subQ6=sQuery(id+"F0.wireOp",EDGE,"E21.filletArc");var subQ7=sQuery(id+"F0.wireOp",EDGE,"E1.top");var subQ8=sQuery(id+"F0.wireOp",EDGE,"E1.left");var subQ9=sQuery(id+"F0.wireOp",EDGE,"E1.right");var subQ10=sQuery(id+"F0.wireOp",EDGE,"E23.filletArc");var subQ11=sQuery(id+"F0.wireOp",EDGE,"E24.filletArc");Q0=makeQuery(id+"F2.boolean.opBoolean","SPLIT",FACE,{"disambiguationData":[TD([makeQuery(id+"F1.opExtrude","SWEPT_FACE",FACE,{"disambiguationData":[OSD([subQ5])]})])],"derivedFrom":makeQuery(id+"F1.opExtrude","CAP_FACE",FACE,{"disambiguationData":[OSD([subQ5,subQ7,subQ8,subQ9,subQ4,subQ3,subQ2,subQ1,subQ6,subQ0,subQ10,subQ11])],"isStart":true})});}
            var sketch = newSketch(context, id + "F16", { "sketchPlane" : qUnion([Q0])});
            skLineSegment(sketch, "E79", {"start": v(0, 90) * mm, "end": v(0, 120) * mm, "construction": true});
            skCircle(sketch, "E80", {"center": v(0, 120) * mm, "radius": 6 * mm});
            skArc(sketch, "E81", {"start": v(15, 120) * mm, "mid": v(0, 135) * mm, "end": v(-15, 120) * mm});
            skLineSegment(sketch, "E82", {"start": v(-15, 120) * mm, "end": v(-15, 108) * mm});
            skLineSegment(sketch, "E83", {"start": v(-15, 108) * mm, "end": v(-33, 90) * mm});
            skLineSegment(sketch, "E84", {"start": v(15, 120) * mm, "end": v(15, 108) * mm});
            skLineSegment(sketch, "E85", {"start": v(15, 108) * mm, "end": v(33, 90) * mm});
            skLineSegment(sketch, "E86", {"start": v(-80, 0) * mm, "end": v(80, 0) * mm, "construction": true});
            skLineSegment(sketch, "E87.MirrorCS", {"start": v(15, -120) * mm, "end": v(15, -108) * mm});
            skLineSegment(sketch, "E88.MirrorCS", {"start": v(-15, -120) * mm, "end": v(-15, -108) * mm});
            skLineSegment(sketch, "E89.MirrorCS", {"start": v(-15, -108) * mm, "end": v(-33, -90) * mm});
            skLineSegment(sketch, "E90.MirrorCS", {"start": v(15, -108) * mm, "end": v(33, -90) * mm});
            skCircle(sketch, "E91.MirrorC", {"center": v(0, -120) * mm, "radius": 6 * mm});
            skLineSegment(sketch, "E92.MirrorCS", {"start": v(0, -90) * mm, "end": v(0, -120) * mm, "construction": true});
            skArc(sketch, "E93.MirrorCS", {"start": v(15, -120) * mm, "mid": v(0, -135) * mm, "end": v(-15, -120) * mm});
            skSolve(sketch);
        }
        {
            var Q0;
            Q0=makeQuery(id+"F16.imprint","IMPRINT",FACE,{"disambiguationData":[TD([[makeQuery(id+"F16.imprint","IMPRINT",EDGE,{"derivedFrom":sQuery(id+"F16.wireOp",EDGE,"E80")}),-1.0]])]});
            var Q1;
            Q1=makeQuery(id+"F16.imprint","IMPRINT",FACE,{"disambiguationData":[TD([[makeQuery(id+"F16.imprint","IMPRINT",EDGE,{"derivedFrom":makeQuery(id+"F1.opExtrude","CAP_EDGE",EDGE,{"disambiguationData":[OSD([sQuery(id+"F0.wireOp",EDGE,"E1.left")])],"isStart":true})}),-1.0]])]});
            var Q2;
            Q2=makeQuery(id+"F16.imprint","IMPRINT",FACE,{"disambiguationData":[TD([[makeQuery(id+"F16.imprint","IMPRINT",EDGE,{"derivedFrom":sQuery(id+"F16.wireOp",EDGE,"E87.MirrorCS")}),1.0]])]});
            var Q3;
            Q3=makeQuery(id+"F2.opExtrude","CAP_FACE",FACE,{"disambiguationData":[OSD([sQuery(id+"F0.wireOp",EDGE,"E12"),sQuery(id+"F0.wireOp",EDGE,"E13"),sQuery(id+"F0.wireOp",EDGE,"E14"),sQuery(id+"F0.wireOp",EDGE,"E15"),sQuery(id+"F0.wireOp",EDGE,"E17.filletArc"),sQuery(id+"F0.wireOp",EDGE,"E18.filletArc"),sQuery(id+"F0.wireOp",EDGE,"E19.filletArc"),sQuery(id+"F0.wireOp",EDGE,"E20.filletArc"),sQuery(id+"F0.wireOp",EDGE,"E25.0"),sQuery(id+"F0.wireOp",EDGE,"E25.1"),sQuery(id+"F0.wireOp",EDGE,"E25.2"),sQuery(id+"F0.wireOp",EDGE,"E25.3"),sQuery(id+"F0.wireOp",EDGE,"E25.4"),sQuery(id+"F0.wireOp",EDGE,"E25.5"),sQuery(id+"F0.wireOp",EDGE,"E25.6"),sQuery(id+"F0.wireOp",EDGE,"E25.7")])],"isStart":false});
            extrude(context, id + "F17", {"entities" : qUnion([Q0, Q1, Q2]), "operationType" : NewBodyOperationType.ADD, "endBound" : BoundingType.UP_TO_SURFACE, "endBoundEntityFace" : qUnion([Q3]), "depth" : 25 * mm});
        }
    });
